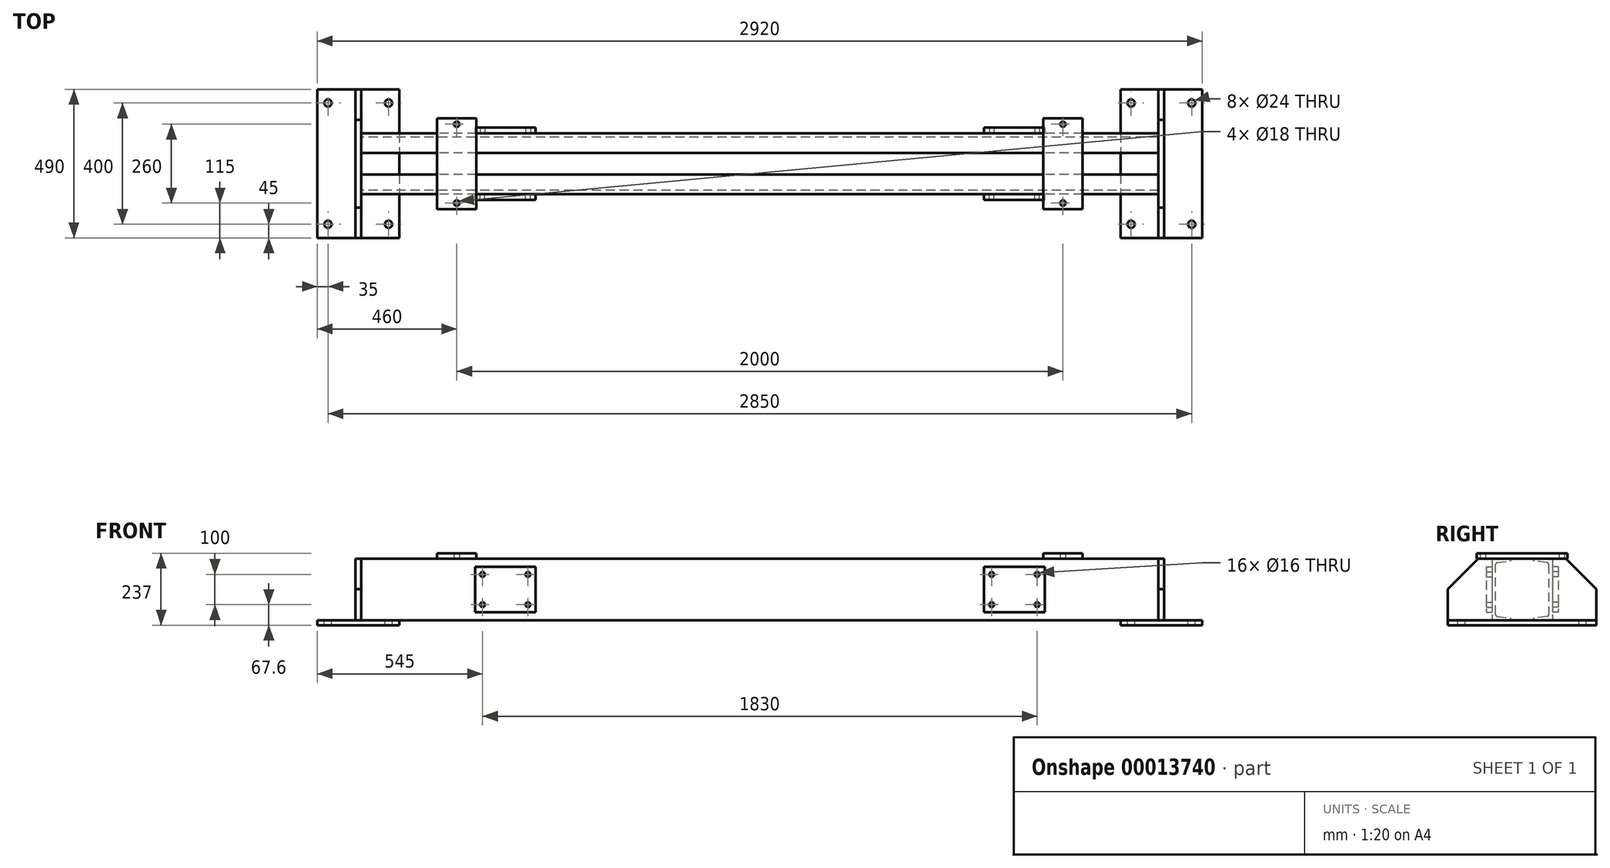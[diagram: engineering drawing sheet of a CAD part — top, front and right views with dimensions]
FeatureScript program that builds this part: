
annotation { "Feature Type Name" : "Feature", "Feature Type Description" : "" }
export const myFeature = defineFeature(function(context is Context, id is Id, definition is map)
    precondition{}
    {
        {
            var Q0;
            Q0=qCreatedBy(makeId("Right.planeOp"),FACE);
            var sketch = newSketch(context, id + "F0", { "sketchPlane" : qUnion([Q0])});
            skLineSegment(sketch, "E0", {"start": v(0, 81.85) * mm, "end": v(0, -95.58) * mm, "construction": true});
            skLineSegment(sketch, "E1", {"start": v(-119.35, 0) * mm, "end": v(122.16, 0) * mm, "construction": true});
            skLineSegment(sketch, "E2.0", {"start": v(-100, 101.6) * mm, "end": v(-100, 0) * mm});
            skLineSegment(sketch, "E3.0", {"start": v(-100, 101.6) * mm, "end": v(-35.8, 101.6) * mm});
            skLineSegment(sketch, "E4.0", {"start": v(-87.6, 82.16) * mm, "end": v(-87.6, 0) * mm});
            skLineSegment(sketch, "E5.0", {"start": v(-35.8, 88.1) * mm, "end": v(122.16, 88.1) * mm, "construction": true});
            skLineSegment(sketch, "E6.0", {"start": v(-35.8, 101.6) * mm, "end": v(-35.8, 99.47) * mm});
            skLineSegment(sketch, "E7", {"start": v(-81.71, 88.9) * mm, "end": v(-40.13, 94.51) * mm});
            skPoint(sketch, "E8.visualSharp", {"position": v(-35.8, 95.1) * mm});
            skArc(sketch, "E8.filletArc", {"start": v(-40.13, 94.51) * mm, "mid": v(-37.04, 96.18) * mm, "end": v(-35.8, 99.47) * mm});
            skPoint(sketch, "E9.visualSharp", {"position": v(-87.6, 88.1) * mm});
            skArc(sketch, "E9.filletArc", {"start": v(-81.71, 88.9) * mm, "mid": v(-85.92, 86.63) * mm, "end": v(-87.6, 82.16) * mm});
            skArc(sketch, "E10.0.MirrorCS", {"start": v(-40.13, -94.51) * mm, "mid": v(-37.04, -96.18) * mm, "end": v(-35.8, -99.47) * mm});
            skLineSegment(sketch, "E10.1.MirrorCS", {"start": v(-35.8, -101.6) * mm, "end": v(-35.8, -99.47) * mm});
            skArc(sketch, "E10.2.MirrorCS", {"start": v(-81.71, -88.9) * mm, "mid": v(-85.92, -86.63) * mm, "end": v(-87.6, -82.16) * mm});
            skPoint(sketch, "E10.3.MirrorP", {"position": v(-87.6, -88.1) * mm});
            skLineSegment(sketch, "E10.4.MirrorCS", {"start": v(-100, -101.6) * mm, "end": v(-100, 0) * mm});
            skLineSegment(sketch, "E10.5.MirrorCS", {"start": v(-87.6, -82.16) * mm, "end": v(-87.6, 0) * mm});
            skLineSegment(sketch, "E10.6.MirrorCS", {"start": v(-81.71, -88.9) * mm, "end": v(-40.13, -94.51) * mm});
            skLineSegment(sketch, "E10.7.MirrorCS", {"start": v(-100, -101.6) * mm, "end": v(-35.8, -101.6) * mm});
            skPoint(sketch, "E10.8.MirrorP", {"position": v(-35.8, -95.1) * mm});
            skLineSegment(sketch, "E11.0.MirrorCS", {"start": v(35.8, -101.6) * mm, "end": v(35.8, -99.47) * mm});
            skArc(sketch, "E11.1.MirrorCS", {"start": v(40.13, 94.51) * mm, "mid": v(37.04, 96.18) * mm, "end": v(35.8, 99.47) * mm});
            skLineSegment(sketch, "E11.2.MirrorCS", {"start": v(35.8, 101.6) * mm, "end": v(35.8, 99.47) * mm});
            skArc(sketch, "E11.3.MirrorCS", {"start": v(40.13, -94.51) * mm, "mid": v(37.04, -96.18) * mm, "end": v(35.8, -99.47) * mm});
            skArc(sketch, "E11.4.MirrorCS", {"start": v(81.71, 88.9) * mm, "mid": v(85.92, 86.63) * mm, "end": v(87.6, 82.16) * mm});
            skArc(sketch, "E11.5.MirrorCS", {"start": v(81.71, -88.9) * mm, "mid": v(85.92, -86.63) * mm, "end": v(87.6, -82.16) * mm});
            skLineSegment(sketch, "E11.6.MirrorCS", {"start": v(100, -101.6) * mm, "end": v(35.8, -101.6) * mm});
            skLineSegment(sketch, "E11.7.MirrorCS", {"start": v(100, -101.6) * mm, "end": v(100, 0) * mm});
            skLineSegment(sketch, "E11.8.MirrorCS", {"start": v(81.71, -88.9) * mm, "end": v(40.13, -94.51) * mm});
            skLineSegment(sketch, "E11.9.MirrorCS", {"start": v(87.6, -82.16) * mm, "end": v(87.6, 0) * mm});
            skPoint(sketch, "E11.10.MirrorP", {"position": v(87.6, -88.1) * mm});
            skPoint(sketch, "E11.11.MirrorP", {"position": v(35.8, 95.1) * mm});
            skPoint(sketch, "E11.12.MirrorP", {"position": v(35.8, -95.1) * mm});
            skLineSegment(sketch, "E11.13.MirrorCS", {"start": v(81.71, 88.9) * mm, "end": v(40.13, 94.51) * mm});
            skLineSegment(sketch, "E11.14.MirrorCS", {"start": v(100, 101.6) * mm, "end": v(35.8, 101.6) * mm});
            skPoint(sketch, "E11.15.MirrorP", {"position": v(87.6, 88.1) * mm});
            skLineSegment(sketch, "E11.16.MirrorCS", {"start": v(100, 101.6) * mm, "end": v(100, 0) * mm});
            skLineSegment(sketch, "E11.17.MirrorCS", {"start": v(87.6, 82.16) * mm, "end": v(87.6, 0) * mm});
            skSolve(sketch);
        }
        {
            var Q0;
            Q0 = qSketchRegion(id + "F0", true);
            extrude(context, id + "F1", {"entities" : qUnion([Q0]), "endBound" : BoundingType.SYMMETRIC, "depth" : 2631 * mm});
        }
        {
            var Q0;
            Q0=makeQuery(id+"F1.opExtrude","CAP_FACE",FACE,{"disambiguationData":[OSD([sQuery(id+"F0.wireOp",EDGE,"E2.0"),sQuery(id+"F0.wireOp",EDGE,"E3.0"),sQuery(id+"F0.wireOp",EDGE,"E4.0"),sQuery(id+"F0.wireOp",EDGE,"E6.0"),sQuery(id+"F0.wireOp",EDGE,"E7"),sQuery(id+"F0.wireOp",EDGE,"E8.filletArc"),sQuery(id+"F0.wireOp",EDGE,"E9.filletArc"),sQuery(id+"F0.wireOp",EDGE,"E10.0.MirrorCS"),sQuery(id+"F0.wireOp",EDGE,"E10.1.MirrorCS"),sQuery(id+"F0.wireOp",EDGE,"E10.2.MirrorCS"),sQuery(id+"F0.wireOp",EDGE,"E10.4.MirrorCS"),sQuery(id+"F0.wireOp",EDGE,"E10.5.MirrorCS"),sQuery(id+"F0.wireOp",EDGE,"E10.6.MirrorCS"),sQuery(id+"F0.wireOp",EDGE,"E10.7.MirrorCS")])],"isStart":false});
            var sketch = newSketch(context, id + "F2", { "sketchPlane" : qUnion([Q0])});
            skLineSegment(sketch, "E12", {"start": v(0, 0) * mm, "end": v(0, -156.9) * mm, "construction": true});
            skLineSegment(sketch, "E13.0", {"start": v(-245, 1.6) * mm, "end": v(-245, -101.6) * mm});
            skLineSegment(sketch, "E14.0", {"start": v(-245, -101.6) * mm, "end": v(0, -101.6) * mm});
            skLineSegment(sketch, "E15.0", {"start": v(-145, 101.6) * mm, "end": v(0, 101.6) * mm});
            skPoint(sketch, "E16.orphan", {"position": v(-100, -101.6) * mm});
            skPoint(sketch, "E17.orphan", {"position": v(-100, 101.6) * mm});
            skPoint(sketch, "E18.orphan", {"position": v(-35.8, 101.6) * mm});
            skPoint(sketch, "E19.orphan", {"position": v(-35.8, -101.6) * mm});
            skLineSegment(sketch, "E20.0", {"start": v(-145, 101.6) * mm, "end": v(-145, -101.6) * mm, "construction": true});
            skLineSegment(sketch, "E21.0", {"start": v(-245, 1.6) * mm, "end": v(0, 1.6) * mm, "construction": true});
            skLineSegment(sketch, "E22", {"start": v(-245, 1.6) * mm, "end": v(-145, 101.6) * mm});
            skLineSegment(sketch, "E23.0.MirrorCS", {"start": v(245, 1.6) * mm, "end": v(245, -101.6) * mm});
            skLineSegment(sketch, "E23.1.MirrorCS", {"start": v(245, -101.6) * mm, "end": v(0, -101.6) * mm});
            skLineSegment(sketch, "E24.0.MirrorCS", {"start": v(245, 1.6) * mm, "end": v(145, 101.6) * mm});
            skLineSegment(sketch, "E25.0.MirrorCS", {"start": v(145, 101.6) * mm, "end": v(0, 101.6) * mm});
            skSolve(sketch);
        }
        {
            var Q0;
            Q0 = qSketchRegion(id + "F2", true);
            extrude(context, id + "F3", {"entities" : qUnion([Q0]), "depth" : 19 * mm});
        }
        {
            var Q0;
            Q0=makeQuery(id+"F3.opExtrude","SWEPT_BODY",BODY,{"disambiguationData":[OSD([sQuery(id+"F2.wireOp",EDGE,"E13.0"),sQuery(id+"F2.wireOp",EDGE,"E14.0"),sQuery(id+"F2.wireOp",EDGE,"E15.0"),sQuery(id+"F2.wireOp",EDGE,"E22"),sQuery(id+"F2.wireOp",EDGE,"E23.0.MirrorCS"),sQuery(id+"F2.wireOp",EDGE,"E23.1.MirrorCS"),sQuery(id+"F2.wireOp",EDGE,"E24.0.MirrorCS"),sQuery(id+"F2.wireOp",EDGE,"E25.0.MirrorCS")])]});
            var Q1;
            Q1=qCreatedBy(makeId("Right.planeOp"),FACE);
            mirror(context, id + "F4", {"entities" : qUnion([Q0]), "mirrorPlane" : qUnion([Q1])});
        }
        {
            var Q0;
            Q0=makeQuery(id+"F1.opExtrude","SWEPT_FACE",FACE,{"disambiguationData":[OSD([sQuery(id+"F0.wireOp",EDGE,"E10.7.MirrorCS")])]});
            var sketch = newSketch(context, id + "F5", { "sketchPlane" : qUnion([Q0])});
            skLineSegment(sketch, "E26", {"start": v(0, 0) * mm, "end": v(0, 513.83) * mm, "construction": true});
            skLineSegment(sketch, "E27", {"start": v(0, 0) * mm, "end": v(1410.8, 0) * mm, "construction": true});
            skLineSegment(sketch, "E28.0", {"start": v(1325, 0) * mm, "end": v(1325, 513.83) * mm, "construction": true});
            skLineSegment(sketch, "E29.0", {"start": v(1460, -245) * mm, "end": v(1460, 245) * mm});
            skLineSegment(sketch, "E30.0", {"start": v(1190, 245) * mm, "end": v(1460, 245) * mm});
            skLineSegment(sketch, "E31.0.MirrorCS", {"start": v(1190, -245) * mm, "end": v(1190, 245) * mm});
            skPoint(sketch, "E32.orphan", {"position": v(1190, 513.83) * mm});
            skPoint(sketch, "E33.orphan", {"position": v(1460, 513.83) * mm});
            skLineSegment(sketch, "E34.0.MirrorCS", {"start": v(1190, -245) * mm, "end": v(1460, -245) * mm});
            skPoint(sketch, "E35.orphan", {"position": v(1460, 0) * mm});
            skPoint(sketch, "E36.orphan", {"position": v(1190, 0) * mm});
            skLineSegment(sketch, "E37.0", {"start": v(0, 200) * mm, "end": v(1425, 200) * mm, "construction": true});
            skLineSegment(sketch, "E38.0", {"start": v(1425, 0) * mm, "end": v(1425, 200) * mm, "construction": true});
            skCircle(sketch, "E39", {"center": v(1425, 200) * mm, "radius": 12 * mm});
            skCircle(sketch, "E40.0.MirrorC", {"center": v(1425, -200) * mm, "radius": 12 * mm});
            skCircle(sketch, "E41.0.MirrorC", {"center": v(1225, -200) * mm, "radius": 12 * mm});
            skCircle(sketch, "E42.0.MirrorC", {"center": v(1225, 200) * mm, "radius": 12 * mm});
            skSolve(sketch);
        }
        {
            var Q0;
            Q0 = qSketchRegion(id + "F5", true);
            extrude(context, id + "F6", {"entities" : qUnion([Q0]), "depth" : 16 * mm});
        }
        {
            var Q0;
            Q0=makeQuery(id+"F6.opExtrude","SWEPT_BODY",BODY,{"disambiguationData":[OSD([sQuery(id+"F5.wireOp",EDGE,"E29.0"),sQuery(id+"F5.wireOp",EDGE,"E30.0"),sQuery(id+"F5.wireOp",EDGE,"E31.0.MirrorCS"),sQuery(id+"F5.wireOp",EDGE,"E34.0.MirrorCS"),sQuery(id+"F5.wireOp",EDGE,"E39"),sQuery(id+"F5.wireOp",EDGE,"E40.0.MirrorC"),sQuery(id+"F5.wireOp",EDGE,"E41.0.MirrorC"),sQuery(id+"F5.wireOp",EDGE,"E42.0.MirrorC")])]});
            var Q1;
            Q1=qCreatedBy(makeId("Right.planeOp"),FACE);
            mirror(context, id + "F7", {"entities" : qUnion([Q0]), "mirrorPlane" : qUnion([Q1])});
        }
        {
            var Q0;
            Q0=makeQuery(id+"F1.opExtrude","SWEPT_FACE",FACE,{"disambiguationData":[OSD([sQuery(id+"F0.wireOp",EDGE,"E11.14.MirrorCS")])]});
            var sketch = newSketch(context, id + "F8", { "sketchPlane" : qUnion([Q0])});
            skLineSegment(sketch, "E43", {"start": v(0, 0) * mm, "end": v(0, 449.39) * mm, "construction": true});
            skLineSegment(sketch, "E44", {"start": v(0, 0) * mm, "end": v(1523.6, 0) * mm, "construction": true});
            skLineSegment(sketch, "E45.0", {"start": v(1000, 0) * mm, "end": v(1000, 449.39) * mm, "construction": true});
            skLineSegment(sketch, "E46.0", {"start": v(1000, 150) * mm, "end": v(1065, 150) * mm});
            skLineSegment(sketch, "E47.0", {"start": v(1065, 0) * mm, "end": v(1065, 150) * mm});
            skLineSegment(sketch, "E48.0.MirrorCS", {"start": v(1065, 0) * mm, "end": v(1065, -150) * mm});
            skLineSegment(sketch, "E49.0.MirrorCS", {"start": v(1000, -150) * mm, "end": v(1065, -150) * mm});
            skLineSegment(sketch, "E50.0.MirrorCS", {"start": v(1000, 150) * mm, "end": v(935, 150) * mm});
            skLineSegment(sketch, "E51.0.MirrorCS", {"start": v(935, 0) * mm, "end": v(935, 150) * mm});
            skLineSegment(sketch, "E52.0.MirrorCS", {"start": v(935, 0) * mm, "end": v(935, -150) * mm});
            skLineSegment(sketch, "E53.0.MirrorCS", {"start": v(1000, -150) * mm, "end": v(935, -150) * mm});
            skLineSegment(sketch, "E54.0", {"start": v(0, 130) * mm, "end": v(1523.6, 130) * mm, "construction": true});
            skCircle(sketch, "E55", {"center": v(1000, 130) * mm, "radius": 9 * mm});
            skCircle(sketch, "E56.0.MirrorC", {"center": v(1000, -130) * mm, "radius": 9 * mm});
            skSolve(sketch);
        }
        {
            var Q0;
            Q0 = qSketchRegion(id + "F8", true);
            extrude(context, id + "F9", {"entities" : qUnion([Q0]), "depth" : 17.8 * mm});
        }
        {
            var Q0;
            Q0=makeQuery(id+"F9.opExtrude","SWEPT_BODY",BODY,{"disambiguationData":[OSD([sQuery(id+"F8.wireOp",EDGE,"E46.0"),sQuery(id+"F8.wireOp",EDGE,"E47.0"),sQuery(id+"F8.wireOp",EDGE,"E48.0.MirrorCS"),sQuery(id+"F8.wireOp",EDGE,"E49.0.MirrorCS"),sQuery(id+"F8.wireOp",EDGE,"E50.0.MirrorCS"),sQuery(id+"F8.wireOp",EDGE,"E51.0.MirrorCS"),sQuery(id+"F8.wireOp",EDGE,"E52.0.MirrorCS"),sQuery(id+"F8.wireOp",EDGE,"E53.0.MirrorCS"),sQuery(id+"F8.wireOp",EDGE,"E55"),sQuery(id+"F8.wireOp",EDGE,"E56.0.MirrorC")])]});
            var Q1;
            Q1=qCreatedBy(makeId("Right.planeOp"),FACE);
            mirror(context, id + "F10", {"entities" : qUnion([Q0]), "mirrorPlane" : qUnion([Q1])});
        }
        {
            var Q0;
            Q0=makeQuery(id+"F1.opExtrude","SWEPT_FACE",FACE,{"disambiguationData":[OSD([sQuery(id+"F0.wireOp",EDGE,"E11.7.MirrorCS"),sQuery(id+"F0.wireOp",EDGE,"E11.16.MirrorCS")])]});
            var sketch = newSketch(context, id + "F11", { "sketchPlane" : qUnion([Q0])});
            skLineSegment(sketch, "E57", {"start": v(0, 268.1) * mm, "end": v(0, -305.9) * mm, "construction": true});
            skLineSegment(sketch, "E58", {"start": v(0, 0) * mm, "end": v(-1422.02, 0) * mm, "construction": true});
            skLineSegment(sketch, "E59.0", {"start": v(-840, 268.1) * mm, "end": v(-840, -305.9) * mm, "construction": true});
            skLineSegment(sketch, "E60.0", {"start": v(-840, 75) * mm, "end": v(-940, 75) * mm});
            skLineSegment(sketch, "E61.0", {"start": v(-940, 75) * mm, "end": v(-940, 0) * mm});
            skLineSegment(sketch, "E62.0.MirrorCS", {"start": v(-840, 75) * mm, "end": v(-740, 75) * mm});
            skLineSegment(sketch, "E63.0.MirrorCS", {"start": v(-740, 75) * mm, "end": v(-740, 0) * mm});
            skLineSegment(sketch, "E64.0.MirrorCS", {"start": v(-940, -75) * mm, "end": v(-940, 0) * mm});
            skLineSegment(sketch, "E65.0.MirrorCS", {"start": v(-840, -75) * mm, "end": v(-940, -75) * mm});
            skLineSegment(sketch, "E66.0.MirrorCS", {"start": v(-840, -75) * mm, "end": v(-740, -75) * mm});
            skLineSegment(sketch, "E67.0.MirrorCS", {"start": v(-740, -75) * mm, "end": v(-740, 0) * mm});
            skLineSegment(sketch, "E68.0", {"start": v(-915, 268.1) * mm, "end": v(-915, -305.9) * mm, "construction": true});
            skLineSegment(sketch, "E69.0", {"start": v(0, 50) * mm, "end": v(-1422.02, 50) * mm, "construction": true});
            skCircle(sketch, "E70", {"center": v(-915, 50) * mm, "radius": 8 * mm});
            skCircle(sketch, "E71.0.MirrorC", {"center": v(-765, 50) * mm, "radius": 8 * mm});
            skCircle(sketch, "E72.0.MirrorC", {"center": v(-915, -50) * mm, "radius": 8 * mm});
            skCircle(sketch, "E73.0.MirrorC", {"center": v(-765, -50) * mm, "radius": 8 * mm});
            skCircle(sketch, "E74.0.MirrorC", {"center": v(915, 50) * mm, "radius": 8 * mm});
            skLineSegment(sketch, "E74.1.MirrorCS", {"start": v(840, 75) * mm, "end": v(940, 75) * mm});
            skCircle(sketch, "E74.2.MirrorC", {"center": v(765, 50) * mm, "radius": 8 * mm});
            skCircle(sketch, "E74.3.MirrorC", {"center": v(915, -50) * mm, "radius": 8 * mm});
            skCircle(sketch, "E74.4.MirrorC", {"center": v(765, -50) * mm, "radius": 8 * mm});
            skLineSegment(sketch, "E74.5.MirrorCS", {"start": v(740, -75) * mm, "end": v(740, 0) * mm});
            skLineSegment(sketch, "E74.6.MirrorCS", {"start": v(840, 268.1) * mm, "end": v(840, -305.9) * mm, "construction": true});
            skLineSegment(sketch, "E74.7.MirrorCS", {"start": v(840, -75) * mm, "end": v(740, -75) * mm});
            skLineSegment(sketch, "E74.8.MirrorCS", {"start": v(0, 0) * mm, "end": v(1422.02, 0) * mm, "construction": true});
            skLineSegment(sketch, "E74.9.MirrorCS", {"start": v(740, 75) * mm, "end": v(740, 0) * mm});
            skLineSegment(sketch, "E74.10.MirrorCS", {"start": v(940, 75) * mm, "end": v(940, 0) * mm});
            skLineSegment(sketch, "E74.11.MirrorCS", {"start": v(840, 75) * mm, "end": v(740, 75) * mm});
            skLineSegment(sketch, "E74.12.MirrorCS", {"start": v(940, -75) * mm, "end": v(940, 0) * mm});
            skLineSegment(sketch, "E74.13.MirrorCS", {"start": v(0, 50) * mm, "end": v(1422.02, 50) * mm, "construction": true});
            skLineSegment(sketch, "E74.14.MirrorCS", {"start": v(915, 268.1) * mm, "end": v(915, -305.9) * mm, "construction": true});
            skLineSegment(sketch, "E74.15.MirrorCS", {"start": v(840, -75) * mm, "end": v(940, -75) * mm});
            skSolve(sketch);
        }
        {
            var Q0;
            Q0 = qSketchRegion(id + "F11", true);
            extrude(context, id + "F12", {"entities" : qUnion([Q0]), "depth" : 19 * mm});
        }
        {
            var Q0;
            Q0=makeQuery(id+"F12.opExtrude","SWEPT_BODY",BODY,{"disambiguationData":[OSD([sQuery(id+"F11.wireOp",EDGE,"E60.0"),sQuery(id+"F11.wireOp",EDGE,"E61.0"),sQuery(id+"F11.wireOp",EDGE,"E62.0.MirrorCS"),sQuery(id+"F11.wireOp",EDGE,"E63.0.MirrorCS"),sQuery(id+"F11.wireOp",EDGE,"E64.0.MirrorCS"),sQuery(id+"F11.wireOp",EDGE,"E65.0.MirrorCS"),sQuery(id+"F11.wireOp",EDGE,"E66.0.MirrorCS"),sQuery(id+"F11.wireOp",EDGE,"E67.0.MirrorCS"),sQuery(id+"F11.wireOp",EDGE,"E70"),sQuery(id+"F11.wireOp",EDGE,"E71.0.MirrorC"),sQuery(id+"F11.wireOp",EDGE,"E72.0.MirrorC"),sQuery(id+"F11.wireOp",EDGE,"E73.0.MirrorC")])]});
            var Q1;
            Q1=makeQuery(id+"F12.opExtrude","SWEPT_BODY",BODY,{"disambiguationData":[OSD([sQuery(id+"F11.wireOp",EDGE,"E74.0.MirrorC"),sQuery(id+"F11.wireOp",EDGE,"E74.1.MirrorCS"),sQuery(id+"F11.wireOp",EDGE,"E74.2.MirrorC"),sQuery(id+"F11.wireOp",EDGE,"E74.3.MirrorC"),sQuery(id+"F11.wireOp",EDGE,"E74.4.MirrorC"),sQuery(id+"F11.wireOp",EDGE,"E74.5.MirrorCS"),sQuery(id+"F11.wireOp",EDGE,"E74.7.MirrorCS"),sQuery(id+"F11.wireOp",EDGE,"E74.9.MirrorCS"),sQuery(id+"F11.wireOp",EDGE,"E74.10.MirrorCS"),sQuery(id+"F11.wireOp",EDGE,"E74.11.MirrorCS"),sQuery(id+"F11.wireOp",EDGE,"E74.12.MirrorCS"),sQuery(id+"F11.wireOp",EDGE,"E74.15.MirrorCS")])]});
            var Q2;
            Q2=qCreatedBy(makeId("Front.planeOp"),FACE);
            mirror(context, id + "F13", {"entities" : qUnion([Q0, Q1]), "mirrorPlane" : qUnion([Q2])});
        }
    });
